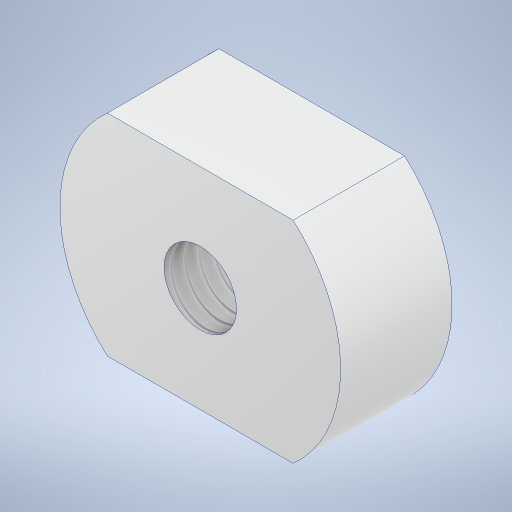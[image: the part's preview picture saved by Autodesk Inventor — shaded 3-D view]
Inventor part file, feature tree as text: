
AUTODESK INVENTOR PART (.ipt)
format: ipt  version: 2024 (Build 280153000, 153)  size: 227,840 bytes
history: native  units: mm
features: sketch x2, extrude x1, hole x1
ambient origin geometry x8: Origin, YZ Plane, XZ Plane, XY Plane, X Axis, Y Axis, Z Axis, Center Point
bodies: Solid1 (feature_tree)
feature tree (4):
  extrude  "Extrusion1"  Depth=12.0mm
  hole  "Hole1"  [1 undecoded]
  sketch  "Sketch1"  dims[d0=16.0mm d1=12.0mm]
  sketch  "Sketch2"  dims[d2=6.35mm d3=0.0mm d4=4.134mm d5=10.0mm d6=4.0mm d7=2.0mm d8=90.0deg d9=8.0mm d10=20.594885mm]
note: 1 required parameter value undecoded (feature->parameter linkage not recoverable at this tier; creation-order binding heuristic only, values carry confidence <= 0.55)
